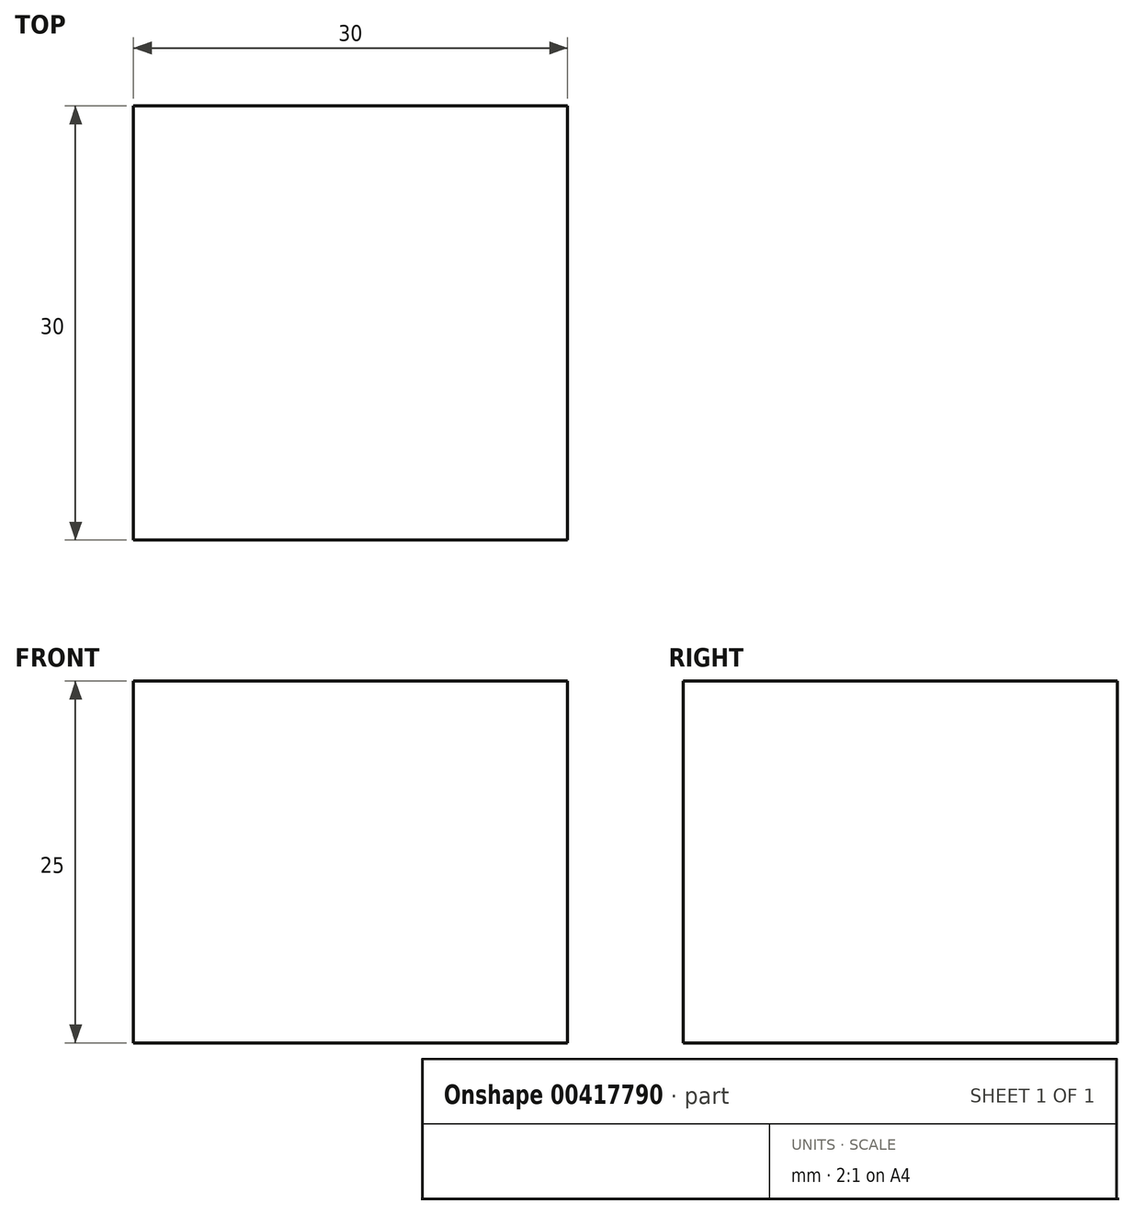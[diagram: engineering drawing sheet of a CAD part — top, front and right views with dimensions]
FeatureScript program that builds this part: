
annotation { "Feature Type Name" : "Feature", "Feature Type Description" : "" }
export const myFeature = defineFeature(function(context is Context, id is Id, definition is map)
    precondition{}
    {
        {
            var Q0;
            Q0=qCreatedBy(makeId("Top.planeOp"),FACE);
            var sketch = newSketch(context, id + "F0", { "sketchPlane" : qUnion([Q0])});
            skLineSegment(sketch, "E0.bottom", {"start": v(-15, 15) * mm, "end": v(15, 15) * mm});
            skLineSegment(sketch, "E0.top", {"start": v(-15, -15) * mm, "end": v(15, -15) * mm});
            skLineSegment(sketch, "E0.left", {"start": v(-15, 15) * mm, "end": v(-15, -15) * mm});
            skLineSegment(sketch, "E0.right", {"start": v(15, 15) * mm, "end": v(15, -15) * mm});
            skPoint(sketch, "E0.middle", {"position": v(0, 0) * mm});
            skSolve(sketch);
        }
        {
            var Q0;
            Q0=makeQuery(id+"F0.imprint","IMPRINT",FACE,{"disambiguationData":[TD([[makeQuery(id+"F0.imprint","IMPRINT",EDGE,{"derivedFrom":sQuery(id+"F0.wireOp",EDGE,"E0.bottom")}),-1.0]])]});
            extrude(context, id + "F1", {"entities" : qUnion([Q0]), "depth" : 25 * mm});
        }
    });
